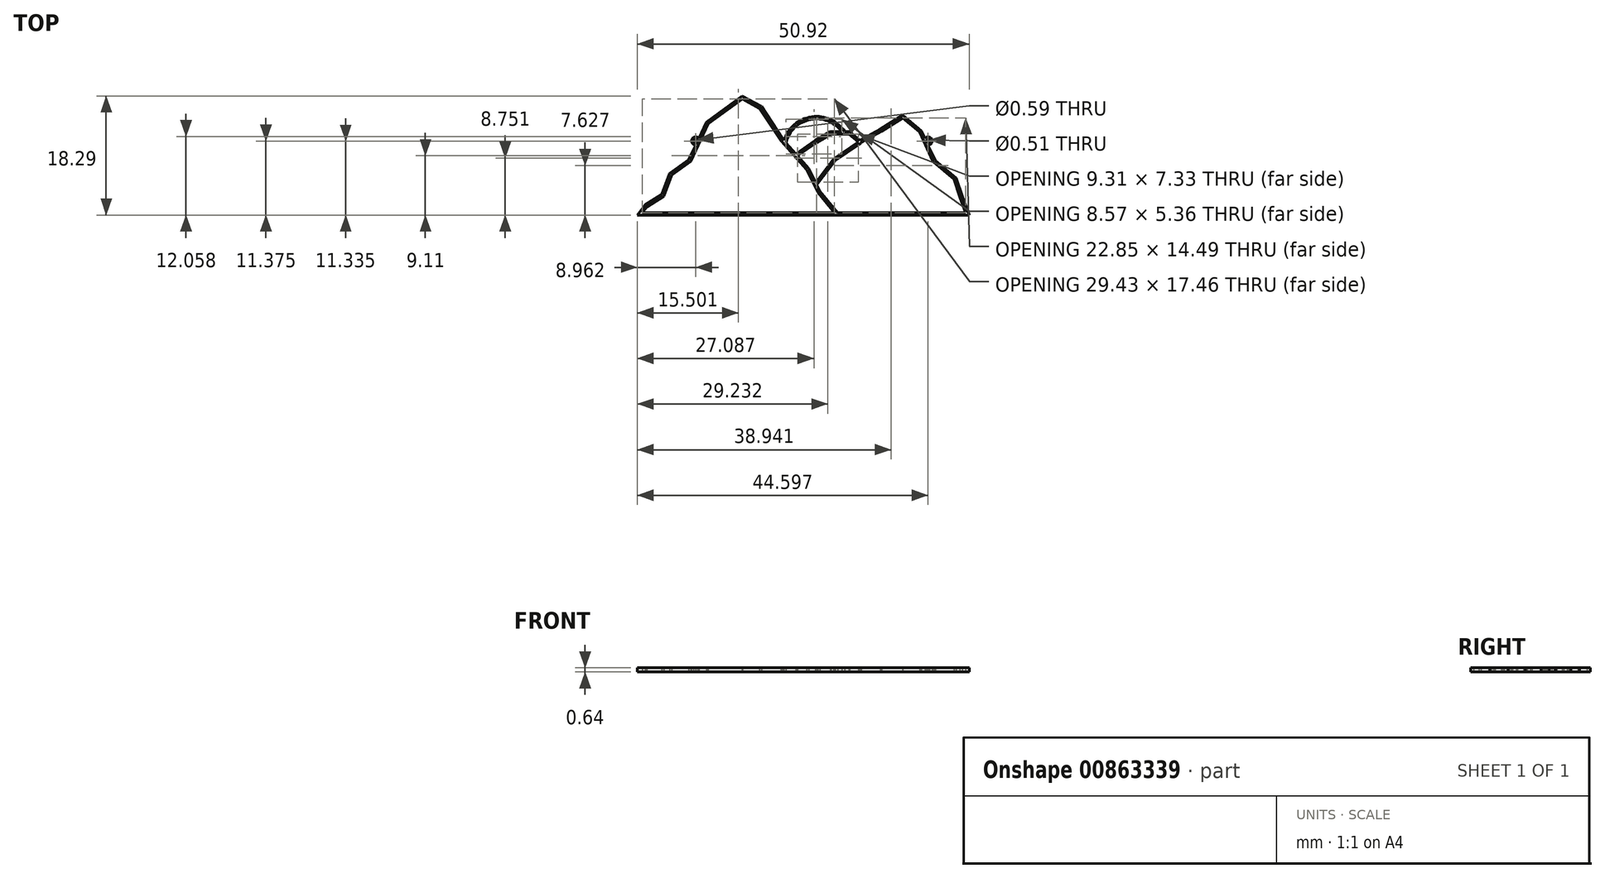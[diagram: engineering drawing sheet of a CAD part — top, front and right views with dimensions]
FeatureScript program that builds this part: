
annotation { "Feature Type Name" : "Feature", "Feature Type Description" : "" }
export const myFeature = defineFeature(function(context is Context, id is Id, definition is map)
    precondition{}
    {
        {
            var Q0;
            Q0=qCreatedBy(makeId("Top.planeOp"),FACE);
            var sketch = newSketch(context, id + "F0", { "sketchPlane" : qUnion([Q0])});
            skLineSegment(sketch, "E0", {"start": v(-31.02, 0) * mm, "end": v(-29.81, 1.54) * mm});
            skLineSegment(sketch, "E1", {"start": v(-29.81, 1.54) * mm, "end": v(-27.27, 3.15) * mm});
            skLineSegment(sketch, "E2", {"start": v(-27.27, 3.15) * mm, "end": v(-26.06, 6.36) * mm});
            skLineSegment(sketch, "E3", {"start": v(-26.06, 6.36) * mm, "end": v(-23.11, 8.5) * mm});
            skLineSegment(sketch, "E4", {"start": v(-23.11, 8.5) * mm, "end": v(-22.07, 10.74) * mm});
            skLineSegment(sketch, "E5", {"start": v(-20.43, 14.27) * mm, "end": v(-14.94, 18.29) * mm});
            skLineSegment(sketch, "E6", {"start": v(-14.94, 18.29) * mm, "end": v(-12, 16.68) * mm});
            skLineSegment(sketch, "E7", {"start": v(-12, 16.68) * mm, "end": v(-8.64, 11.59) * mm});
            skLineSegment(sketch, "E8", {"start": v(-8.64, 11.59) * mm, "end": v(-8.52, 11.45) * mm});
            skLineSegment(sketch, "E9", {"start": v(-4.76, 7.17) * mm, "end": v(-3.72, 5.1) * mm});
            skLineSegment(sketch, "E10", {"start": v(-3.01, 3.68) * mm, "end": v(-0.31, 0.38) * mm});
            skLineSegment(sketch, "E11", {"start": v(-6.7, 9.38) * mm, "end": v(-3.68, 11.46) * mm});
            skLineSegment(sketch, "E12", {"start": v(-3.68, 11.46) * mm, "end": v(-1.4, 12.8) * mm});
            skLineSegment(sketch, "E13", {"start": v(-1.4, 12.8) * mm, "end": v(0.35, 12.8) * mm});
            skLineSegment(sketch, "E14", {"start": v(1.54, 12.8) * mm, "end": v(3.15, 11.46) * mm});
            skLineSegment(sketch, "E15", {"start": v(3.15, 11.46) * mm, "end": v(6.23, 13.2) * mm});
            skLineSegment(sketch, "E16", {"start": v(6.23, 13.2) * mm, "end": v(9.71, 15.34) * mm});
            skLineSegment(sketch, "E17", {"start": v(9.71, 15.34) * mm, "end": v(12.57, 12.96) * mm});
            skLineSegment(sketch, "E18", {"start": v(12.57, 12.96) * mm, "end": v(13.35, 11.27) * mm});
            skLineSegment(sketch, "E19", {"start": v(14.67, 8.37) * mm, "end": v(17.86, 5.72) * mm});
            skLineSegment(sketch, "E20", {"start": v(17.86, 5.72) * mm, "end": v(18.82, 2.88) * mm});
            skLineSegment(sketch, "E21", {"start": v(18.82, 2.88) * mm, "end": v(19.9, 0) * mm});
            skLineSegment(sketch, "E22", {"start": v(19.9, 0) * mm, "end": v(-31.02, 0) * mm});
            skArc(sketch, "E23", {"start": v(0.82, 12.8) * mm, "mid": v(-4.28, 15.08) * mm, "end": v(-8.52, 11.45) * mm});
            skLineSegment(sketch, "E24.0", {"start": v(-22.8, 8.26) * mm, "end": v(-20.13, 14.02) * mm});
            skLineSegment(sketch, "E24.1", {"start": v(-30.23, 0.38) * mm, "end": v(-29.55, 1.25) * mm});
            skLineSegment(sketch, "E24.2", {"start": v(-29.55, 1.25) * mm, "end": v(-26.95, 2.9) * mm});
            skLineSegment(sketch, "E24.3", {"start": v(-26.95, 2.9) * mm, "end": v(-25.74, 6.12) * mm});
            skLineSegment(sketch, "E24.4", {"start": v(-25.74, 6.12) * mm, "end": v(-22.8, 8.26) * mm});
            skLineSegment(sketch, "E25.0", {"start": v(-20.13, 14.02) * mm, "end": v(-14.9, 17.84) * mm});
            skLineSegment(sketch, "E26.0", {"start": v(-14.9, 17.84) * mm, "end": v(-12.26, 16.4) * mm});
            skLineSegment(sketch, "E27.0", {"start": v(-12.26, 16.4) * mm, "end": v(-8.96, 11.38) * mm});
            skLineSegment(sketch, "E28.0", {"start": v(-8.93, 11.34) * mm, "end": v(-5.08, 6.95) * mm});
            skLineSegment(sketch, "E29.0", {"start": v(-5.08, 6.95) * mm, "end": v(-3.36, 3.51) * mm});
            skLineSegment(sketch, "E30.0", {"start": v(-3.3, 3.44) * mm, "end": v(-0.8, 0.38) * mm});
            skLineSegment(sketch, "E31", {"start": v(-30.23, 0.38) * mm, "end": v(-0.8, 0.38) * mm});
            skLineSegment(sketch, "E32", {"start": v(-8.96, 11.38) * mm, "end": v(-8.93, 11.34) * mm});
            skLineSegment(sketch, "E33", {"start": v(-3.36, 3.51) * mm, "end": v(-3.3, 3.44) * mm});
            skArc(sketch, "E34", {"start": v(-3.72, 5.1) * mm, "mid": v(-3.67, 5.09) * mm, "end": v(-3.62, 5.09) * mm});
            skArc(sketch, "E35.trimOffspring", {"start": v(0.35, 12.8) * mm, "mid": v(-4.47, 14.66) * mm, "end": v(-8.22, 11.1) * mm});
            skLineSegment(sketch, "E36.0", {"start": v(-1.3, 12.41) * mm, "end": v(1.54, 12.41) * mm});
            skLineSegment(sketch, "E36.1", {"start": v(-3.48, 11.13) * mm, "end": v(-1.3, 12.41) * mm});
            skLineSegment(sketch, "E36.2", {"start": v(-6.48, 9.06) * mm, "end": v(-3.48, 11.13) * mm});
            skLineSegment(sketch, "E37.0", {"start": v(1.3, 12.5) * mm, "end": v(2.87, 11.2) * mm});
            skLineSegment(sketch, "E38.trimOffspring", {"start": v(-8.22, 11.1) * mm, "end": v(-6.7, 9.38) * mm});
            skLineSegment(sketch, "E39.trimOffspring", {"start": v(-6.45, 9.1) * mm, "end": v(-4.76, 7.17) * mm});
            skPoint(sketch, "E40.orphan", {"position": v(-3.68, 5.02) * mm});
            skLineSegment(sketch, "E41.trimOffspring", {"start": v(-3.5, 4.67) * mm, "end": v(-3.01, 3.68) * mm});
            skLineSegment(sketch, "E42.trimOffspring", {"start": v(0.82, 12.8) * mm, "end": v(1.54, 12.8) * mm});
            skLineSegment(sketch, "E43.0", {"start": v(6.42, 12.87) * mm, "end": v(9.68, 14.87) * mm});
            skLineSegment(sketch, "E43.1", {"start": v(3.34, 11.12) * mm, "end": v(6.42, 12.87) * mm});
            skLineSegment(sketch, "E44.0", {"start": v(9.68, 14.87) * mm, "end": v(12.26, 12.72) * mm});
            skLineSegment(sketch, "E45.0", {"start": v(12.26, 12.72) * mm, "end": v(14.32, 8.22) * mm});
            skLineSegment(sketch, "E46.0", {"start": v(14.43, 8.08) * mm, "end": v(17.53, 5.5) * mm});
            skLineSegment(sketch, "E47.0", {"start": v(17.53, 5.5) * mm, "end": v(18.46, 2.76) * mm});
            skLineSegment(sketch, "E48.0", {"start": v(18.47, 2.75) * mm, "end": v(19.35, 0.38) * mm});
            skLineSegment(sketch, "E49", {"start": v(18.46, 2.76) * mm, "end": v(18.47, 2.75) * mm});
            skLineSegment(sketch, "E50", {"start": v(-0.31, 0.38) * mm, "end": v(19.35, 0.38) * mm});
            skLineSegment(sketch, "E51", {"start": v(3.13, 10.91) * mm, "end": v(3.34, 11.12) * mm});
            skLineSegment(sketch, "E52", {"start": v(14.32, 8.22) * mm, "end": v(14.43, 8.08) * mm});
            skLineSegment(sketch, "E53", {"start": v(-3.62, 5.09) * mm, "end": v(-0.92, 8.64) * mm});
            skLineSegment(sketch, "E54", {"start": v(-0.92, 8.64) * mm, "end": v(2.87, 11.2) * mm});
            skLineSegment(sketch, "E55.0", {"start": v(-0.66, 8.36) * mm, "end": v(3.08, 10.88) * mm});
            skLineSegment(sketch, "E55.1", {"start": v(-3.31, 4.86) * mm, "end": v(-0.66, 8.36) * mm});
            skLineSegment(sketch, "E56", {"start": v(3.08, 10.88) * mm, "end": v(3.13, 10.91) * mm});
            skLineSegment(sketch, "E57", {"start": v(-3.5, 4.67) * mm, "end": v(-3.31, 4.86) * mm});
            skLineSegment(sketch, "E58", {"start": v(-38.62, 11.37) * mm, "end": v(38.63, 11.37) * mm, "construction": true});
            skArc(sketch, "E59", {"start": v(13.59, 10.74) * mm, "mid": v(14.15, 11.64) * mm, "end": v(13.1, 11.8) * mm});
            skCircle(sketch, "E60", {"center": v(13.58, 11.37) * mm, "radius": 0.25 * mm});
            skCircle(sketch, "E61", {"center": v(-22.06, 11.33) * mm, "radius": 0.3 * mm});
            skLineSegment(sketch, "E62.trimOffspring", {"start": v(-21.78, 11.37) * mm, "end": v(-21.77, 11.4) * mm});
            skLineSegment(sketch, "E63.trimOffspring", {"start": v(-21.58, 11.8) * mm, "end": v(-20.43, 14.27) * mm});
            skArc(sketch, "E64.trimOffspring", {"start": v(-21.58, 11.8) * mm, "mid": v(-22.63, 11.64) * mm, "end": v(-22.07, 10.74) * mm});
            skLineSegment(sketch, "E65.trimOffspring", {"start": v(13.59, 10.74) * mm, "end": v(14.67, 8.37) * mm});
            skSolve(sketch);
        }
        {
            var Q0;
            Q0=makeQuery(id+"F0.imprint","IMPRINT",FACE,{"disambiguationData":[TD([[makeQuery(id+"F0.imprint","IMPRINT",EDGE,{"derivedFrom":sQuery(id+"F0.wireOp",EDGE,"E0")}),-1.0]])]});
            extrude(context, id + "F1", {"entities" : qUnion([Q0]), "depth" : 0.64 * mm, "offsetDistance" : 25.4 * mm});
        }
    });
